# Revit family: 9220-1-BKS-BBOV-H38-FMTE-BLANCO
name_source: partatom
category: Mechanical Equipment
revit_build: Autodesk Revit MEP 2016 (Build: 20150220_1215(x64)
units: mm (PartAtom-declared; Revit-internal decimal feet)

## family parameters
Cut with Voids When Loaded = Yes
Host = Face
OmniClass Number = 23.45.05.14.34
OmniClass Title = Security Plumbing Fixtures
Part Type = Normal
Room Calculation Point = No
Round Connector Dimension = Use Diameter
Shared = Yes

## types (1)
- 9220-1-BKS-BBOV-H38-FMTE-BLANCO
    Amperage = 0
    CW Connection = Yes
    Default Elevation = 34 "
    Description = Configurable Slab
    HW Connection = Yes
    Manufacturer = Neo-Metro
    Material = BLANCO RESIN
    Model = 9220-1-BKS-BBOV-H38-FMTE-BLANCO
    OVERALL DEPTH = 22
    OVERALL SIZE HEIGHT = 34
    OVERALL SIZE WIDTH = 30
    Revised Date = 12/16/19
    Tempered Water Connection = No
    URL = https://www.neo-metro.com
    Vent Connection = No
    Voltage = 0
    Waste Connection = Yes

## geometry (parser evidence)
native form markers: Sweep x6
no freeform markers — native parametric forms only
